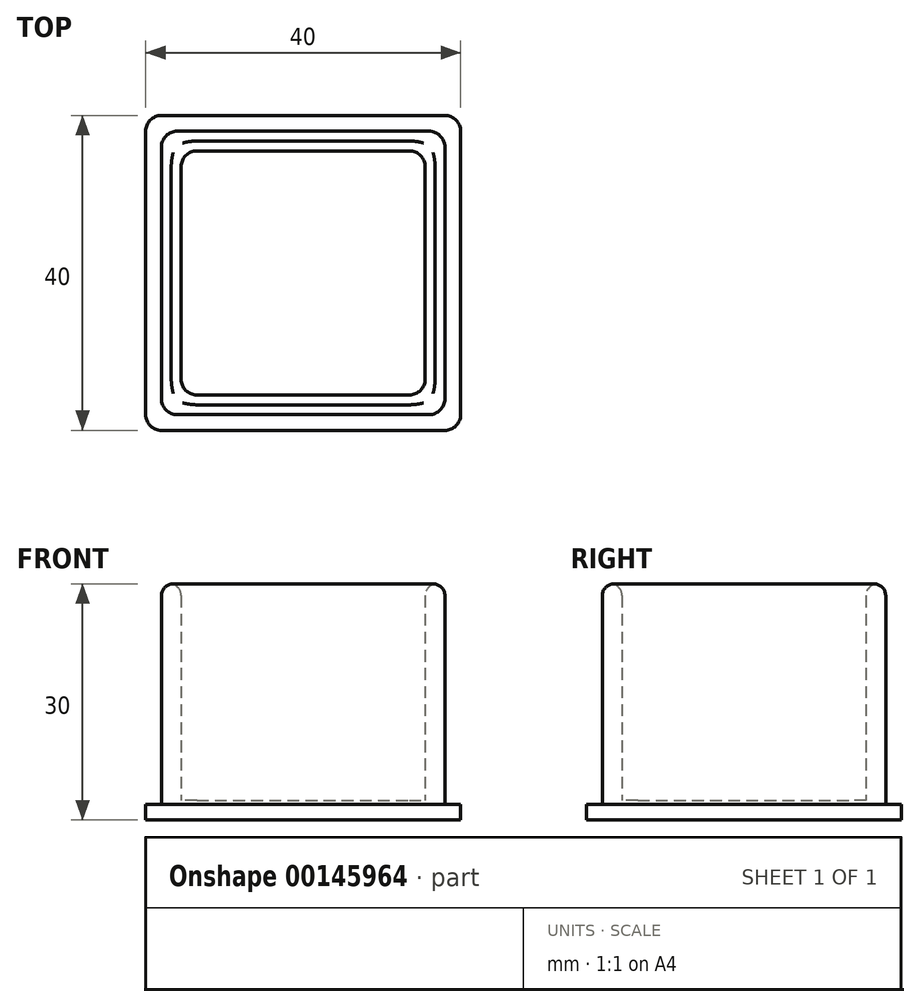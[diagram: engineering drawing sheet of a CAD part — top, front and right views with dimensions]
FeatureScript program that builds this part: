
annotation { "Feature Type Name" : "Feature", "Feature Type Description" : "" }
export const myFeature = defineFeature(function(context is Context, id is Id, definition is map)
    precondition{}
    {
        {
            var Q0;
            Q0=qCreatedBy(makeId("Top.planeOp"),FACE);
            var sketch = newSketch(context, id + "F0", { "sketchPlane" : qUnion([Q0])});
            skLineSegment(sketch, "E0.bottom", {"start": v(18, 20) * mm, "end": v(-18, 20) * mm});
            skLineSegment(sketch, "E0.top", {"start": v(18, -20) * mm, "end": v(-18, -20) * mm});
            skLineSegment(sketch, "E0.left", {"start": v(20, 18) * mm, "end": v(20, -18) * mm});
            skLineSegment(sketch, "E0.right", {"start": v(-20, 18) * mm, "end": v(-20, -18) * mm});
            skPoint(sketch, "E0.middle", {"position": v(0, 0) * mm});
            skLineSegment(sketch, "E1.bottom", {"start": v(18, 18) * mm, "end": v(-18, 18) * mm});
            skLineSegment(sketch, "E1.top", {"start": v(18, -18) * mm, "end": v(-18, -18) * mm});
            skLineSegment(sketch, "E1.left", {"start": v(18, 18) * mm, "end": v(18, -18) * mm});
            skLineSegment(sketch, "E1.right", {"start": v(-18, 18) * mm, "end": v(-18, -18) * mm});
            skPoint(sketch, "E2.visualSharp", {"position": v(-20, 20) * mm});
            skArc(sketch, "E2.filletArc", {"start": v(-18, 20) * mm, "mid": v(-19.41, 19.41) * mm, "end": v(-20, 18) * mm});
            skPoint(sketch, "E3.visualSharp", {"position": v(20, 20) * mm});
            skArc(sketch, "E3.filletArc", {"start": v(20, 18) * mm, "mid": v(19.41, 19.41) * mm, "end": v(18, 20) * mm});
            skPoint(sketch, "E4.visualSharp", {"position": v(20, -20) * mm});
            skArc(sketch, "E4.filletArc", {"start": v(18, -20) * mm, "mid": v(19.41, -19.41) * mm, "end": v(20, -18) * mm});
            skPoint(sketch, "E5.visualSharp", {"position": v(-20, -20) * mm});
            skArc(sketch, "E5.filletArc", {"start": v(-20, -18) * mm, "mid": v(-19.41, -19.41) * mm, "end": v(-18, -20) * mm});
            skSolve(sketch);
        }
        {
            var Q0;
            Q0=makeQuery(id+"F0.imprint","IMPRINT",FACE,{"disambiguationData":[TD([[makeQuery(id+"F0.imprint","IMPRINT",EDGE,{"derivedFrom":sQuery(id+"F0.wireOp",EDGE,"E0.bottom")}),1.0]])]});
            extrude(context, id + "F1", {"entities" : qUnion([Q0]), "depth" : 2 * mm});
        }
        {
            var Q0;
            Q0=makeQuery(id+"F0.imprint","IMPRINT",FACE,{"disambiguationData":[TD([[makeQuery(id+"F0.imprint","IMPRINT",EDGE,{"derivedFrom":sQuery(id+"F0.wireOp",EDGE,"E1.bottom")}),1.0]])]});
            extrude(context, id + "F2", {"entities" : qUnion([Q0]), "operationType" : NewBodyOperationType.ADD, "depth" : 30 * mm});
        }
        {
            var Q0;
            Q0=makeQuery(id+"F2.opExtrude","CAP_FACE",FACE,{"disambiguationData":[OSD([sQuery(id+"F0.wireOp",EDGE,"E1.bottom"),sQuery(id+"F0.wireOp",EDGE,"E1.top"),sQuery(id+"F0.wireOp",EDGE,"E1.left"),sQuery(id+"F0.wireOp",EDGE,"E1.right")])],"isStart":false});
            shell(context, id + "F3", {"entities" : qUnion([Q0]), "thickness" : 2.5 * mm});
        }
        {
            var Q0;
            Q0=makeQuery(id+"F2.opExtrude","SWEPT_EDGE",EDGE,{"disambiguationData":[OSD([sQuery(id+"F0.wireOp",EDGE,"E1.top"),sQuery(id+"F0.wireOp",EDGE,"E1.right")])]});
            var Q1;
            Q1=makeQuery(id+"F2.opExtrude","SWEPT_EDGE",EDGE,{"disambiguationData":[OSD([sQuery(id+"F0.wireOp",EDGE,"E1.bottom"),sQuery(id+"F0.wireOp",EDGE,"E1.left")])]});
            var Q2;
            Q2=makeQuery(id+"F2.opExtrude","SWEPT_EDGE",EDGE,{"disambiguationData":[OSD([sQuery(id+"F0.wireOp",EDGE,"E1.bottom"),sQuery(id+"F0.wireOp",EDGE,"E1.right")])]});
            var Q3;
            Q3=makeQuery(id+"F2.opExtrude","SWEPT_EDGE",EDGE,{"disambiguationData":[OSD([sQuery(id+"F0.wireOp",EDGE,"E1.top"),sQuery(id+"F0.wireOp",EDGE,"E1.left")])]});
            var Q4;
            Q4=makeQuery(id+"F3.opShell","OFFSET_EDGE",EDGE,{"disambiguationData":[OSD([sQuery(id+"F0.wireOp",EDGE,"E1.top"),sQuery(id+"F0.wireOp",EDGE,"E1.right")])]});
            var Q5;
            Q5=makeQuery(id+"F3.opShell","OFFSET_EDGE",EDGE,{"disambiguationData":[OSD([sQuery(id+"F0.wireOp",EDGE,"E1.top"),sQuery(id+"F0.wireOp",EDGE,"E1.left")])]});
            var Q6;
            Q6=makeQuery(id+"F3.opShell","OFFSET_EDGE",EDGE,{"disambiguationData":[OSD([sQuery(id+"F0.wireOp",EDGE,"E1.bottom"),sQuery(id+"F0.wireOp",EDGE,"E1.left")])]});
            var Q7;
            Q7=makeQuery(id+"F3.opShell","OFFSET_EDGE",EDGE,{"disambiguationData":[OSD([sQuery(id+"F0.wireOp",EDGE,"E1.bottom"),sQuery(id+"F0.wireOp",EDGE,"E1.right")])]});
            fillet(context, id + "F4", {"entities" : qUnion([Q0, Q1, Q2, Q3, Q4, Q5, Q6, Q7]), "radius" : 2 * mm, "tangentPropagation" : true, "allowEdgeOverflow" : false});
        }
        {
            var Q0;
            Q0=makeQuery(id+"F2.opExtrude","CAP_EDGE",EDGE,{"disambiguationData":[OSD([sQuery(id+"F0.wireOp",EDGE,"E1.right")])],"isStart":false});
            var Q1;
            Q1=makeQuery(id+"F3.opShell","OFFSET_EDGE",EDGE,{"disambiguationData":[OSD([sQuery(id+"F0.wireOp",EDGE,"E1.right")])]});
            fillet(context, id + "F5", {"entities" : qUnion([Q0, Q1]), "radius" : 1.5 * mm, "tangentPropagation" : true, "allowEdgeOverflow" : false});
        }
    });
